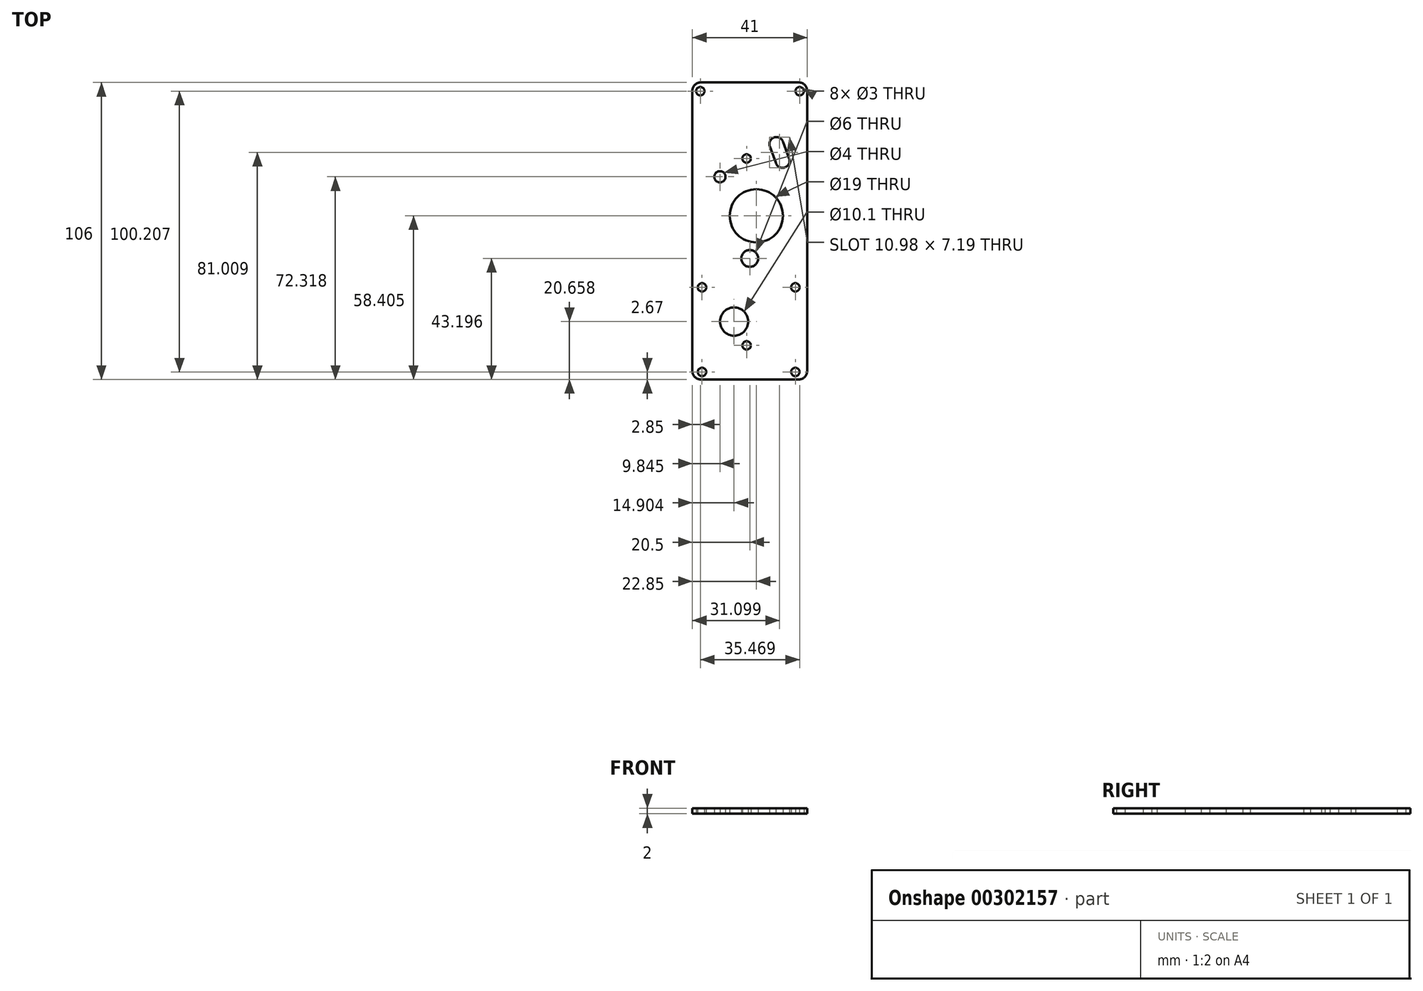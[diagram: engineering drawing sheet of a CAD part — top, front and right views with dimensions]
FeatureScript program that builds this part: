
annotation { "Feature Type Name" : "Feature", "Feature Type Description" : "" }
export const myFeature = defineFeature(function(context is Context, id is Id, definition is map)
    precondition{}
    {
        {
            var Q0;
            Q0=qCreatedBy(makeId("Top.planeOp"),FACE);
            var sketch = newSketch(context, id + "F0", { "sketchPlane" : qUnion([Q0])});
            skCircle(sketch, "E0", {"center": v(-18.23, -51.47) * mm, "radius": 1.5 * mm});
            skCircle(sketch, "E1", {"center": v(-18.23, -21.27) * mm, "radius": 1.5 * mm});
            skLineSegment(sketch, "E2.bottom", {"start": v(-21.68, 51.86) * mm, "end": v(19.32, 51.86) * mm});
            skLineSegment(sketch, "E2.top", {"start": v(-21.68, -54.14) * mm, "end": v(19.32, -54.14) * mm});
            skLineSegment(sketch, "E2.left", {"start": v(-21.68, 51.86) * mm, "end": v(-21.68, -54.14) * mm});
            skLineSegment(sketch, "E2.right", {"start": v(19.32, 51.86) * mm, "end": v(19.32, -54.14) * mm});
            skArc(sketch, "E3", {"start": v(-8.05, 46.53) * mm, "mid": v(-4.94, 40.84) * mm, "end": v(1, 38.21) * mm});
            skLineSegment(sketch, "E4", {"start": v(1, 38.21) * mm, "end": v(1, 28.21) * mm});
            skLineSegment(sketch, "E5", {"start": v(-11.86, 33.21) * mm, "end": v(22.45, 33.21) * mm, "construction": true});
            skArc(sketch, "E6.MirrorCS", {"start": v(-8.05, 19.89) * mm, "mid": v(-4.94, 25.58) * mm, "end": v(1, 28.21) * mm});
            skCircle(sketch, "E7", {"center": v(-2.3, 41.71) * mm, "radius": 1.5 * mm});
            skCircle(sketch, "E8.MirrorC", {"center": v(-2.3, 24.71) * mm, "radius": 1.5 * mm});
            skCircle(sketch, "E9", {"center": v(-6.78, 33.21) * mm, "radius": 5.05 * mm});
            skLineSegment(sketch, "E10", {"start": v(-28.15, -0.14) * mm, "end": v(20.86, -0.14) * mm, "construction": true});
            skCircle(sketch, "E11.MirrorC", {"center": v(-2.3, -24.98) * mm, "radius": 1.5 * mm});
            skArc(sketch, "E12.MirrorCS", {"start": v(-8.05, -20.16) * mm, "mid": v(-4.94, -25.86) * mm, "end": v(1, -28.48) * mm});
            skLineSegment(sketch, "E13.MirrorCS", {"start": v(1, -38.48) * mm, "end": v(1, -28.48) * mm});
            skArc(sketch, "E14.MirrorCS", {"start": v(-8.05, -46.8) * mm, "mid": v(-4.94, -41.1) * mm, "end": v(1, -38.48) * mm});
            skCircle(sketch, "E15.MirrorC", {"center": v(-2.3, -41.98) * mm, "radius": 1.5 * mm});
            skCircle(sketch, "E16.MirrorC", {"center": v(-6.78, -33.48) * mm, "radius": 5.05 * mm});
            skLineSegment(sketch, "E17", {"start": v(-4.93, -17.22) * mm, "end": v(-4.93, -48.35) * mm, "construction": true});
            skLineSegment(sketch, "E18", {"start": v(10, -20.52) * mm, "end": v(10, -46.52) * mm});
            skLineSegment(sketch, "E19", {"start": v(10, -46.52) * mm, "end": v(-8.05, -46.8) * mm});
            skLineSegment(sketch, "E20", {"start": v(10, -20.52) * mm, "end": v(-8.05, -20.16) * mm});
            skLineSegment(sketch, "E21.MirrorCS", {"start": v(10, 20.25) * mm, "end": v(-8.05, 19.89) * mm});
            skLineSegment(sketch, "E22.MirrorCS", {"start": v(10, 20.25) * mm, "end": v(10, 46.25) * mm});
            skLineSegment(sketch, "E23.MirrorCS", {"start": v(10, 46.25) * mm, "end": v(-8.05, 46.53) * mm});
            skCircle(sketch, "E24", {"center": v(1.17, 4.26) * mm, "radius": 9.5 * mm});
            skCircle(sketch, "E25", {"center": v(10.52, 23.86) * mm, "radius": 2.5 * mm});
            skCircle(sketch, "E26", {"center": v(-11.84, -0.14) * mm, "radius": 2 * mm});
            skCircle(sketch, "E27", {"center": v(-11.84, -18.45) * mm, "radius": 2 * mm});
            skCircle(sketch, "E28.MirrorC", {"center": v(-11.84, 18.18) * mm, "radius": 2 * mm});
            skCircle(sketch, "E29", {"center": v(8.32, 29.86) * mm, "radius": 2.5 * mm});
            skLineSegment(sketch, "E30", {"start": v(10.69, 30.66) * mm, "end": v(12.87, 24.73) * mm});
            skLineSegment(sketch, "E31", {"start": v(8.27, 22.78) * mm, "end": v(5.97, 29) * mm});
            skCircle(sketch, "E32", {"center": v(-1.18, -10.94) * mm, "radius": 3 * mm});
            skCircle(sketch, "E33", {"center": v(-18.83, 48.74) * mm, "radius": 1.5 * mm});
            skCircle(sketch, "E34", {"center": v(15.09, -21.27) * mm, "radius": 1.5 * mm});
            skCircle(sketch, "E35", {"center": v(15.09, -51.47) * mm, "radius": 1.5 * mm});
            skCircle(sketch, "E36", {"center": v(16.64, 48.74) * mm, "radius": 1.5 * mm});
            skSolve(sketch);
        }
        {
            var Q0;
            Q0=makeQuery(id+"F0.imprint","IMPRINT",FACE,{"disambiguationData":[TD([[makeQuery(id+"F0.imprint","IMPRINT",EDGE,{"derivedFrom":sQuery(id+"F0.wireOp",EDGE,"5e25448f-ad87-4180-8a74-d3dedaf74bf8")}),-1.0]])]});
            var Q1;
            Q1=makeQuery(id+"F0.imprint","IMPRINT",FACE,{"disambiguationData":[TD([[makeQuery(id+"F0.imprint","IMPRINT",EDGE,{"derivedFrom":sQuery(id+"F0.wireOp",EDGE,"E3")}),1.0]])]});
            var Q2;
            Q2=makeQuery(id+"F0.imprint","IMPRINT",FACE,{"disambiguationData":[TD([[makeQuery(id+"F0.imprint","IMPRINT",EDGE,{"derivedFrom":sQuery(id+"F0.wireOp",EDGE,"E27")}),1.0]])]});
            var Q3;
            Q3=makeQuery(id+"F0.imprint","IMPRINT",FACE,{"disambiguationData":[TD([[makeQuery(id+"F0.imprint","IMPRINT",EDGE,{"derivedFrom":sQuery(id+"F0.wireOp",EDGE,"E11.MirrorC")}),-1.0]])]});
            var Q4;
            Q4=makeQuery(id+"F0.imprint","IMPRINT",FACE,{"disambiguationData":[TD([[makeQuery(id+"F0.imprint","IMPRINT",EDGE,{"derivedFrom":sQuery(id+"F0.wireOp",EDGE,"E26")}),1.0]])]});
            var Q5;
            Q5=makeQuery(id+"F0.imprint","IMPRINT",FACE,{"disambiguationData":[TD([[makeQuery(id+"F0.imprint","IMPRINT",EDGE,{"derivedFrom":sQuery(id+"F0.wireOp",EDGE,"E28.MirrorC")}),-1.0]])]});
            var Q6;
            Q6=makeQuery(id+"F0.imprint","IMPRINT",FACE,{"disambiguationData":[TD([[makeQuery(id+"F0.imprint","IMPRINT",EDGE,{"derivedFrom":sQuery(id+"F0.wireOp",EDGE,"E0")}),-1.0]])]});
            var Q7;
            Q7=makeQuery(id+"F0.imprint","IMPRINT",FACE,{"disambiguationData":[TD([[makeQuery(id+"F0.imprint","IMPRINT",EDGE,{"derivedFrom":sQuery(id+"F0.wireOp",EDGE,"E9")}),1.0]])]});
            var Q8;
            Q8=makeQuery(id+"F0.imprint","IMPRINT",FACE,{"disambiguationData":[TD([[makeQuery(id+"F0.imprint","IMPRINT",EDGE,{"derivedFrom":sQuery(id+"F0.wireOp",EDGE,"E16.MirrorC")}),-1.0]])]});
            var Q9;
            Q9=makeQuery(id+"F0.imprint","IMPRINT",FACE,{"disambiguationData":[TD([[makeQuery(id+"F0.imprint","IMPRINT",EDGE,{"derivedFrom":sQuery(id+"F0.wireOp",EDGE,"E11.MirrorC")}),1.0]])]});
            var Q10;
            Q10=makeQuery(id+"F0.imprint","IMPRINT",FACE,{"disambiguationData":[TD([[makeQuery(id+"F0.imprint","IMPRINT",EDGE,{"derivedFrom":sQuery(id+"F0.wireOp",EDGE,"E15.MirrorC")}),-1.0]])]});
            var Q11;
            Q11=makeQuery(id+"F0.imprint","IMPRINT",FACE,{"disambiguationData":[TD([[makeQuery(id+"F0.imprint","IMPRINT",EDGE,{"derivedFrom":sQuery(id+"F0.wireOp",EDGE,"E8.MirrorC")}),-1.0]])]});
            var Q12;
            Q12=makeQuery(id+"F0.imprint","IMPRINT",FACE,{"disambiguationData":[TD([[makeQuery(id+"F0.imprint","IMPRINT",EDGE,{"derivedFrom":sQuery(id+"F0.wireOp",EDGE,"E7")}),1.0]])]});
            extrude(context, id + "F1", {"entities" : qUnion([Q0, Q1, Q2, Q3, Q4, Q5, Q6, Q7, Q8, Q9, Q10, Q11, Q12]), "depth" : 2 * mm});
        }
        {
            var Q0;
            Q0=makeQuery(id+"F1.opExtrude","SWEPT_EDGE",EDGE,{"disambiguationData":[OSD([sQuery(id+"F0.wireOp",EDGE,"E2.bottom"),sQuery(id+"F0.wireOp",EDGE,"E2.left")])]});
            var Q1;
            Q1=makeQuery(id+"F1.opExtrude","SWEPT_EDGE",EDGE,{"disambiguationData":[OSD([sQuery(id+"F0.wireOp",EDGE,"E2.top"),sQuery(id+"F0.wireOp",EDGE,"E2.left")])]});
            var Q2;
            Q2=makeQuery(id+"F1.opExtrude","SWEPT_EDGE",EDGE,{"disambiguationData":[OSD([sQuery(id+"F0.wireOp",EDGE,"E2.top"),sQuery(id+"F0.wireOp",EDGE,"E2.right")])]});
            var Q3;
            Q3=makeQuery(id+"F1.opExtrude","SWEPT_EDGE",EDGE,{"disambiguationData":[OSD([sQuery(id+"F0.wireOp",EDGE,"E2.bottom"),sQuery(id+"F0.wireOp",EDGE,"E2.right")])]});
            fillet(context, id + "F2", {"entities" : qUnion([Q0, Q1, Q2, Q3]), "radius" : 3 * mm, "tangentPropagation" : true, "allowEdgeOverflow" : false});
        }
    });
